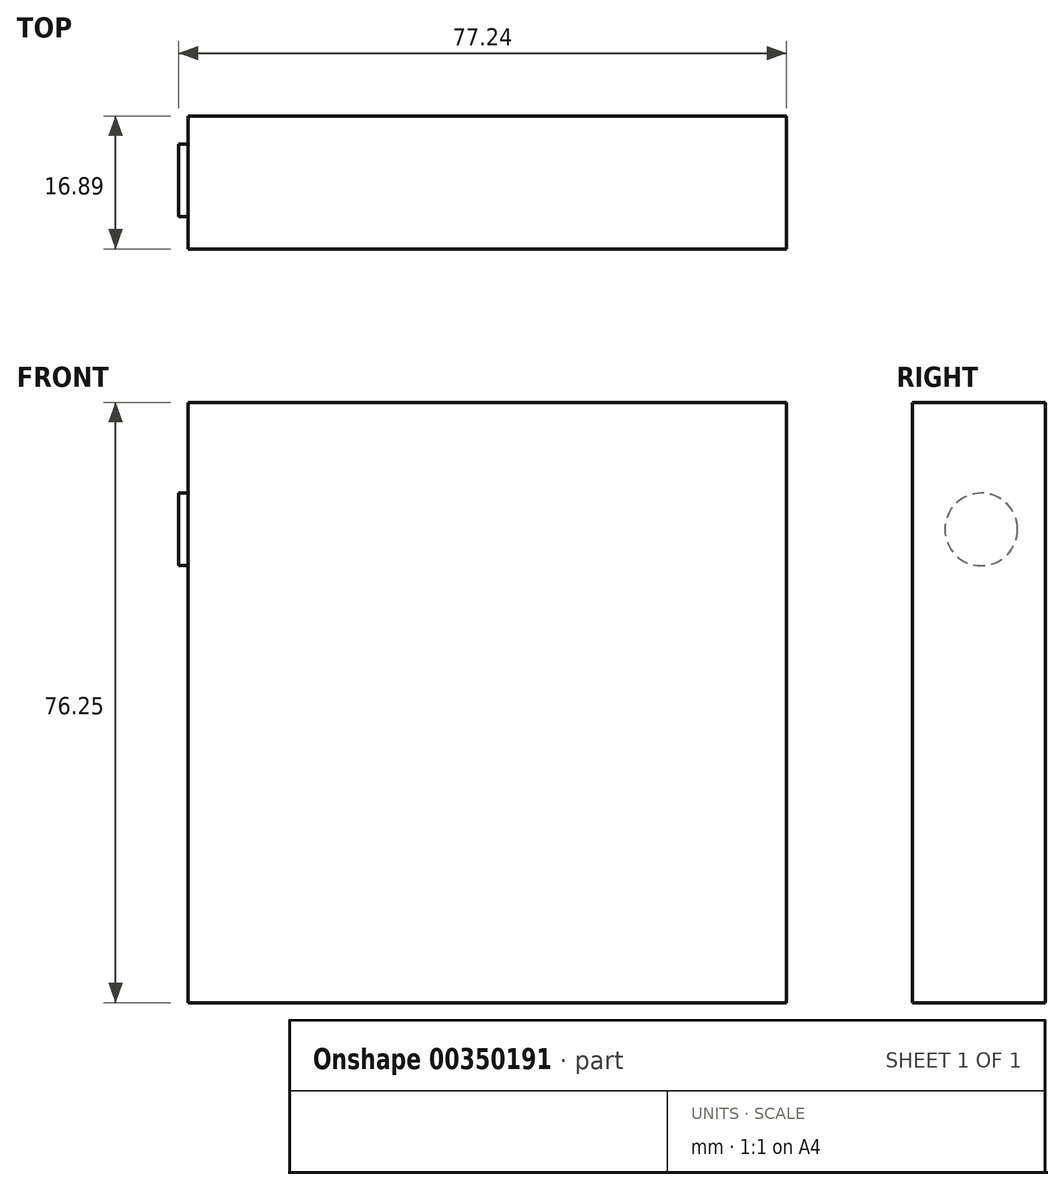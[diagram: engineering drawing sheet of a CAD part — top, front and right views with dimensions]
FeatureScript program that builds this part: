
annotation { "Feature Type Name" : "Feature", "Feature Type Description" : "" }
export const myFeature = defineFeature(function(context is Context, id is Id, definition is map)
    precondition{}
    {
        {
            var Q0;
            Q0=qCreatedBy(makeId("Front.planeOp"),FACE);
            var sketch = newSketch(context, id + "F0", { "sketchPlane" : qUnion([Q0])});
            skLineSegment(sketch, "E0.bottom", {"start": v(-76.03, 76.25) * mm, "end": v(0, 76.25) * mm});
            skLineSegment(sketch, "E0.top", {"start": v(-76.03, 0) * mm, "end": v(0, 0) * mm});
            skLineSegment(sketch, "E0.left", {"start": v(-76.03, 76.25) * mm, "end": v(-76.03, 0) * mm});
            skLineSegment(sketch, "E0.right", {"start": v(0, 76.25) * mm, "end": v(0, 0) * mm});
            skSolve(sketch);
        }
        {
            var Q0;
            Q0=makeQuery(id+"F0.imprint","IMPRINT",FACE,{"disambiguationData":[TD([[makeQuery(id+"F0.imprint","IMPRINT",EDGE,{"derivedFrom":sQuery(id+"F0.wireOp",EDGE,"E0.bottom")}),-1.0]])]});
            extrude(context, id + "F1", {"entities" : qUnion([Q0]), "depth" : 16.9 * mm});
        }
        {
            var Q0;
            Q0=makeQuery(id+"F1.opExtrude","SWEPT_FACE",FACE,{"disambiguationData":[OSD([sQuery(id+"F0.wireOp",EDGE,"E0.left")])]});
            var sketch = newSketch(context, id + "F2", { "sketchPlane" : qUnion([Q0])});
            skCircle(sketch, "E1", {"center": v(8.18, 60.12) * mm, "radius": 4.6 * mm});
            skSolve(sketch);
        }
        {
            var Q0;
            Q0=makeQuery(id+"F2.imprint","IMPRINT",FACE,{"disambiguationData":[TD([[makeQuery(id+"F2.imprint","IMPRINT",EDGE,{"derivedFrom":sQuery(id+"F2.wireOp",EDGE,"E1")}),1.0]])]});
            extrude(context, id + "F3", {"entities" : qUnion([Q0]), "operationType" : NewBodyOperationType.ADD, "depth" : 1.2 * mm});
        }
    });
